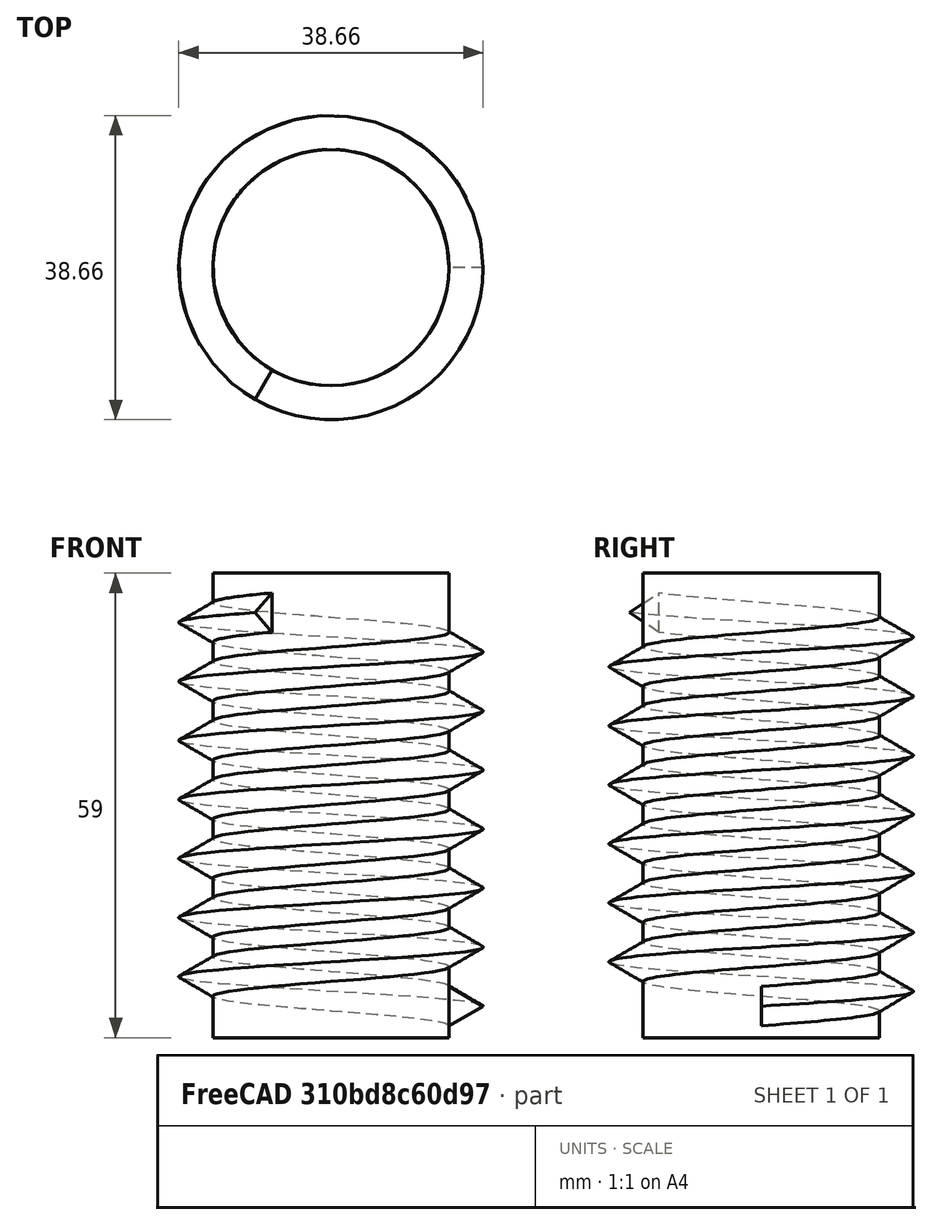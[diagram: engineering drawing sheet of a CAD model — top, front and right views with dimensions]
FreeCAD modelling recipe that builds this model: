
FCSTD DOCUMENT  (FreeCAD 0.18R14445 +26 (Git))
Label: archimedesscrew-techdraw
License: All rights reserved
LicenseURL: http://en.wikipedia.org/wiki/All_rights_reserved
objects: TechDraw::DrawViewDimension×7, TechDraw::DrawProjGroupItem×4, Part::Helix×1, PartDesign::FeatureBase×1, Sketcher::SketchObject×1, PartDesign::AdditivePipe×1, PartDesign::Body×1, Spreadsheet::Sheet×1, TechDraw::DrawSVGTemplate×1, Part::Cylinder×1, Part::MultiFuse×1, TechDraw::DrawProjGroup×1, TechDraw::DrawViewDetail×1, TechDraw::DrawPage×1
note: 8 computed .brp shape members not serialized (recipe doc carries the construction recipe); baked Part::Feature solids carry a one-line shape summary decoded from their .brp

FEATURE [Part::Helix] Helix
  Angle = 0
  AttacherType = Attacher::AttachEngine3D
  Height = 50
  LocalCoord = 0
  Pitch = 7.5
  Radius = 15
  Style = 1
  expr: Pitch = Spreadsheet.pitch
FEATURE [PartDesign::FeatureBase] BaseFeature
  BaseFeature = -> Helix
FEATURE [Sketcher::SketchObject] Sketch
  ExternalGeometry = -> [BaseFeature]
  MapMode = 5
  Placement = pos=(0,0,0) rot=(1,0,0;1.5708rad)
  Support = -> [XZ_Plane]
  sketch-geometry (4):
    g0: LineSegment StartX=19.3301 StartY=0 StartZ=0 EndX=12.8349 EndY=3.75 EndZ=0
    g1: LineSegment StartX=12.8349 StartY=3.75 StartZ=0 EndX=12.8349 EndY=-3.75 EndZ=0
    g2: LineSegment StartX=12.8349 StartY=-3.75 StartZ=0 EndX=19.3301 EndY=0 EndZ=0
    g3: Circle [constr] CenterX=15 CenterY=0 CenterZ=0 NormalX=0 NormalY=0 NormalZ=1 AngleXU=0 Radius=4.33013
  constraints (11):
    c: Coincident(g0,g1)
    c: Coincident(g1,g2)
    c: Coincident(g2,g0)
    c: Equal(g0,g1)
    c: Equal(g0,g2)
    c: PointOnObject(g0,g3)
    c: PointOnObject(g1,g3)
    c: PointOnObject(g2,g3)
    c: Coincident(g3,g-3)
    c: Vertical(g1)
    c: DistanceY(g1,g1) = 7.5
FEATURE [PartDesign::AdditivePipe] AdditivePipe
  AuxilleryCurvelinear = true
  AuxillerySpineTangent = false
  BaseFeature = -> BaseFeature
  Binormal = (0,0,0)
  Mode = 2
  Profile = -> Sketch
  Spine = -> BaseFeature [Edge1,Edge2,Edge3,Edge4,Edge5,Edge6,Edge7]
  SpineTangent = false
  Transformation = 0
  Transition = 0
FEATURE [PartDesign::Body] Body
  BaseFeature = -> Helix
  Group = -> [BaseFeature,Sketch,AdditivePipe]
  Origin = -> Origin
  Tip = -> AdditivePipe
FEATURE [Spreadsheet::Sheet] Spreadsheet
  cells = A2=Pitch; B2(pitch)=7.5; A3=Height; B3(height)=50; A4=Radius; B4(radius)=15
FEATURE [TechDraw::DrawSVGTemplate] Template
  EditableTexts = Designed_by_Name=Archimedes; Drawing_number=1; FC-Date=255 BCE; FC-SC=1:1; FC-SH=1; FC-Title=Screw; Weight=N/A
  Height = 210
  Orientation = 1
  Width = 297
FEATURE [Part::Cylinder] Cylinder
  Angle = 360
  AttacherType = Attacher::AttachEngine3D
  Height = 59
  Placement = pos=(0,0,-4) rot=(0,0,1;0rad)
  Radius = 15
FEATURE [Part::MultiFuse] Fusion
  Placement = pos=(0,0,5) rot=(0,0,1;0rad)
  Shapes = -> [Body,Cylinder]
FEATURE [TechDraw::DrawProjGroupItem] ProjItem  label="Front"
  CoarseView = false
  Direction = (0,-1,0)
  Focus = 100
  HardHidden = false
  IsoCount = 0
  IsoHidden = false
  IsoVisible = false
  LockPosition = false
  Perspective = false
  Rotation = 0
  RotationVector = (1,0,0)
  ScaleType = 0
  SeamHidden = false
  SeamVisible = false
  SmoothHidden = false
  SmoothVisible = false
  Source = -> [Fusion]
  Type = 0
  X = 0
  Y = 0
FEATURE [TechDraw::DrawProjGroupItem] ProjItem001  label="FrontBottomLeft"
  CoarseView = false
  Direction = (-1,-1,-1)
  Focus = 100
  HardHidden = false
  IsoCount = 0
  IsoHidden = false
  IsoVisible = false
  LockPosition = false
  Perspective = false
  Rotation = 0
  RotationVector = (1,1,0)
  ScaleType = 0
  SeamHidden = false
  SeamVisible = false
  SmoothHidden = false
  SmoothVisible = false
  Source = -> [Fusion]
  Type = 8
  X = 80.4938
  Y = 80.4938
FEATURE [TechDraw::DrawProjGroupItem] ProjItem002  label="Bottom"
  CoarseView = false
  Direction = (0,0,-1)
  Focus = 100
  HardHidden = false
  IsoCount = 0
  IsoHidden = false
  IsoVisible = false
  LockPosition = false
  Perspective = false
  Rotation = 0
  RotationVector = (1,0,0)
  ScaleType = 0
  SeamHidden = false
  SeamVisible = false
  SmoothHidden = false
  SmoothVisible = false
  Source = -> [Fusion]
  Type = 5
  X = 0
  Y = 80.4938
FEATURE [TechDraw::DrawProjGroup] ProjGroup001
  Anchor = -> ProjItem
  AutoDistribute = true
  CubeDirs = (1) [(0,0,0)]
  CubeRotations = (1) [(0,0,0)]
  LockPosition = false
  ProjectionType = 0
  Rotation = 0
  ScaleType = 0
  Source = -> [Fusion]
  Views = -> [ProjItem001,ProjItem,ProjItem002]
  X = 45.966
  Y = 75.6675
  spacingX = 15
  spacingY = 15
FEATURE [TechDraw::DrawProjGroupItem] ProjItem003  label="Front001"
  CoarseView = false
  Direction = (0,-1,0)
  Focus = 100
  HardHidden = false
  IsoCount = 0
  IsoHidden = false
  IsoVisible = false
  LockPosition = false
  Perspective = false
  Rotation = 0
  RotationVector = (1,0,0)
  ScaleType = 0
  SeamHidden = false
  SeamVisible = false
  SmoothHidden = false
  SmoothVisible = false
  Source = -> [AdditivePipe]
  Type = 0
  X = 0
  Y = 0
FEATURE [TechDraw::DrawViewDimension] Dimension
  Arbitrary = false
  FormatSpec = %.2f
  LockPosition = false
  MeasureType = 1
  References2D = -> [ProjItem001]
  Rotation = 0
  ScaleType = 0
  Type = 5
  X = 0
  Y = 0
FEATURE [TechDraw::DrawViewDimension] Dimension001
  Arbitrary = false
  FormatSpec = %.2f
  LockPosition = false
  MeasureType = 1
  References2D = -> [ProjItem001]
  Rotation = 0
  ScaleType = 0
  Type = 5
  X = 0
  Y = 0
FEATURE [TechDraw::DrawViewDimension] Dimension002
  Arbitrary = false
  FormatSpec = %.2f
  LockPosition = false
  MeasureType = 1
  Rotation = 0
  ScaleType = 0
  Type = 4
  X = 20.2472
  Y = 25.18
FEATURE [TechDraw::DrawViewDimension] Dimension003
  Arbitrary = false
  FormatSpec = %.2f
  LockPosition = false
  MeasureType = 1
  Rotation = 0
  ScaleType = 0
  Type = 1
  X = 34.0049
  Y = 17.1323
FEATURE [TechDraw::DrawViewDimension] Dimension004
  Arbitrary = false
  FormatSpec = %.2f
  LockPosition = false
  MeasureType = 1
  References2D = -> [ProjItem]
  Rotation = 0
  ScaleType = 0
  Type = 2
  X = 30.3708
  Y = 0.519159
FEATURE [TechDraw::DrawViewDimension] Dimension005
  Arbitrary = false
  FormatSpec = %.2f
  LockPosition = false
  MeasureType = 1
  References2D = -> [ProjItem]
  Rotation = 0
  ScaleType = 0
  Type = 2
  X = 23.3622
  Y = 38.4178
FEATURE [TechDraw::DrawViewDimension] Dimension006
  Arbitrary = false
  FormatSpec = %.2f
  LockPosition = false
  MeasureType = 1
  Rotation = 0
  ScaleType = 0
  Type = 0
  X = -11.4532
  Y = 44.0356
FEATURE [TechDraw::DrawViewDetail] Detail
  AnchorPoint = (-6,24,0)
  BaseView = -> ProjItem
  CoarseView = false
  Direction = (0,-1,0)
  Focus = 100
  HardHidden = false
  IsoCount = 0
  IsoHidden = false
  IsoVisible = false
  LockPosition = false
  Perspective = false
  Radius = 10
  Reference = 1
  Rotation = 0
  Scale = 2
  ScaleType = 0
  SeamHidden = false
  SeamVisible = false
  SmoothHidden = false
  SmoothVisible = false
  Source = -> [Fusion]
  X = 100.159
  Y = 82.7255
FEATURE [TechDraw::DrawPage] Page
  KeepUpdated = true
  ProjectionType = 0
  Template = -> Template
  Views = -> [ProjGroup001,Dimension,Dimension001,Dimension002,Dimension003,Dimension004,Dimension005,Dimension006,Detail]
